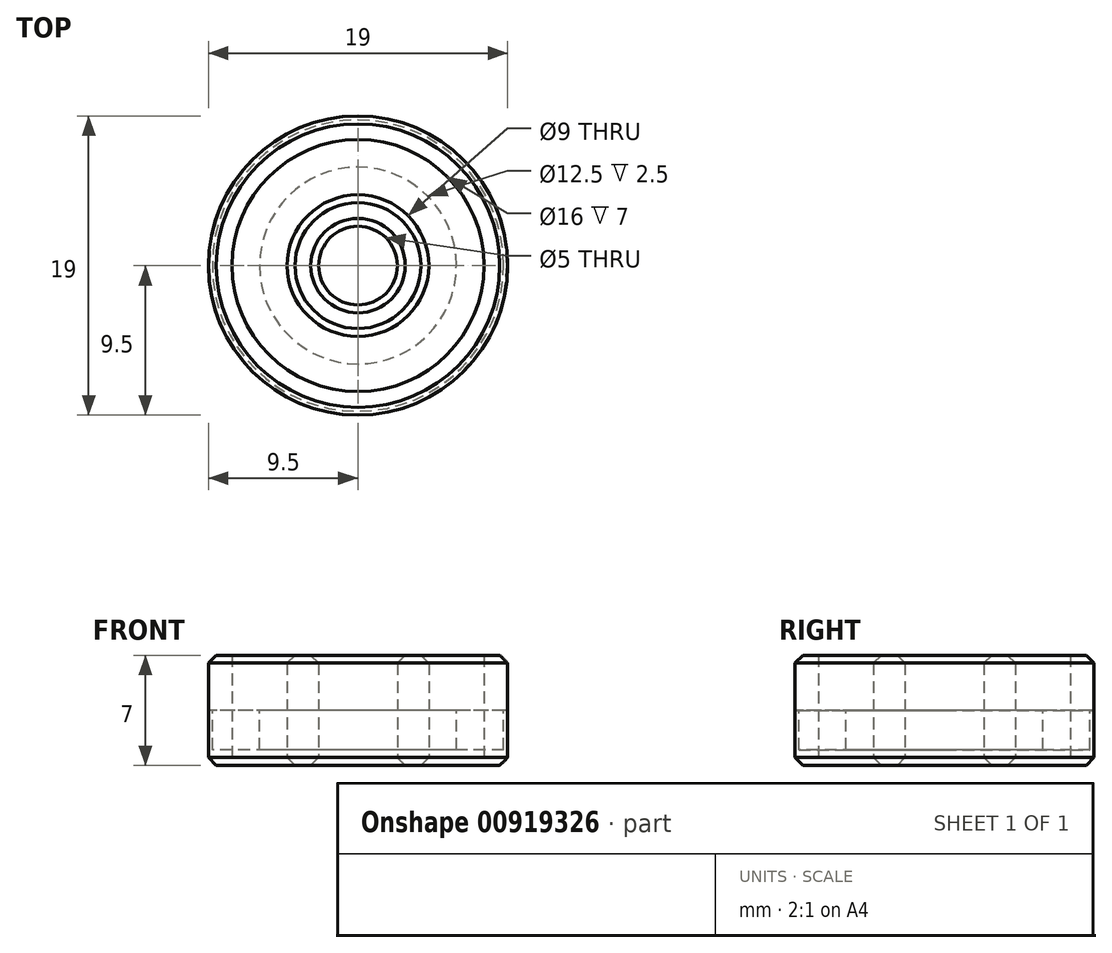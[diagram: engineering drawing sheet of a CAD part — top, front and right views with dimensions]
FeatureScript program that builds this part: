
annotation { "Feature Type Name" : "Feature", "Feature Type Description" : "" }
export const myFeature = defineFeature(function(context is Context, id is Id, definition is map)
    precondition{}
    {
        {
            var Q0;
            Q0=qCreatedBy(makeId("Top.planeOp"),FACE);
            var sketch = newSketch(context, id + "F0", { "sketchPlane" : qUnion([Q0])});
            skCircle(sketch, "E0", {"center": v(0, 0) * mm, "radius": 2.5 * mm});
            skCircle(sketch, "E1", {"center": v(0, 0) * mm, "radius": 4.5 * mm});
            skCircle(sketch, "E2", {"center": v(0, 0) * mm, "radius": 9.5 * mm});
            skCircle(sketch, "E3", {"center": v(0, 0) * mm, "radius": 8 * mm});
            skSolve(sketch);
        }
        {
            var Q0;
            Q0=makeQuery(id+"F0.imprint","IMPRINT",FACE,{"disambiguationData":[TD([[makeQuery(id+"F0.imprint","IMPRINT",EDGE,{"derivedFrom":sQuery(id+"F0.wireOp",EDGE,"E2")}),1.0]])]});
            var Q1;
            Q1=makeQuery(id+"F0.imprint","IMPRINT",FACE,{"disambiguationData":[TD([[makeQuery(id+"F0.imprint","IMPRINT",EDGE,{"derivedFrom":sQuery(id+"F0.wireOp",EDGE,"E0")}),-1.0]])]});
            extrude(context, id + "F1", {"entities" : qUnion([Q0, Q1]), "endBound" : BoundingType.SYMMETRIC, "depth" : 7 * mm, "offsetDistance" : 25 * mm});
        }
        {
            var Q0;
            Q0=qCreatedBy(makeId("Top.planeOp"),FACE);
            var sketch = newSketch(context, id + "F2", { "sketchPlane" : qUnion([Q0])});
            skCircle(sketch, "E4", {"center": v(0, 0) * mm, "radius": 6.25 * mm});
            skCircle(sketch, "E5", {"center": v(0, 0) * mm, "radius": 9.25 * mm});
            skSolve(sketch);
        }
        {
            var Q0;
            Q0=makeQuery(id+"F2.imprint","IMPRINT",FACE,{"disambiguationData":[TD([[makeQuery(id+"F2.imprint","IMPRINT",EDGE,{"derivedFrom":sQuery(id+"F2.wireOp",EDGE,"E4")}),-1.0]])]});
            extrude(context, id + "F3", {"entities" : qUnion([Q0]), "oppositeDirection" : true, "depth" : 2.5 * mm, "offsetDistance" : 25 * mm});
        }
        {
            var Q0;
            Q0=qCreatedBy(makeId("Top.planeOp"),FACE);
            var sketch = newSketch(context, id + "F4", { "sketchPlane" : qUnion([Q0])});
            skCircle(sketch, "E6", {"center": v(0, 0) * mm, "radius": 4.5 * mm});
            skCircle(sketch, "E7", {"center": v(0, 0) * mm, "radius": 9.45 * mm});
            skSolve(sketch);
        }
        {
            var Q0;
            Q0=qSketchRegion(id+"F4",true);
            extrude(context, id + "F5", {"entities" : qUnion([Q0]), "depth" : 3 * mm, "offsetDistance" : 25 * mm});
        }
        {
            var Q0;
            Q0=makeQuery(id+"F1.opExtrude","CAP_EDGE",EDGE,{"disambiguationData":[OSD([sQuery(id+"F0.wireOp",EDGE,"E2")])],"isStart":false});
            var Q1;
            Q1=makeQuery(id+"F1.opExtrude","CAP_EDGE",EDGE,{"disambiguationData":[OSD([sQuery(id+"F0.wireOp",EDGE,"E2")])],"isStart":true});
            var Q2;
            Q2=makeQuery(id+"F1.opExtrude","CAP_EDGE",EDGE,{"disambiguationData":[OSD([sQuery(id+"F0.wireOp",EDGE,"E1")])],"isStart":false});
            var Q3;
            Q3=makeQuery(id+"F1.opExtrude","CAP_EDGE",EDGE,{"disambiguationData":[OSD([sQuery(id+"F0.wireOp",EDGE,"E0")])],"isStart":false});
            var Q4;
            Q4=makeQuery(id+"F1.opExtrude","CAP_EDGE",EDGE,{"disambiguationData":[OSD([sQuery(id+"F0.wireOp",EDGE,"E1")])],"isStart":true});
            var Q5;
            Q5=makeQuery(id+"F1.opExtrude","CAP_EDGE",EDGE,{"disambiguationData":[OSD([sQuery(id+"F0.wireOp",EDGE,"E0")])],"isStart":true});
            chamfer(context, id + "F6", {"entities" : qUnion([Q0, Q1, Q2, Q3, Q4, Q5]), "width" : 0.5 * mm, "tangentPropagation" : true});
        }
    });
